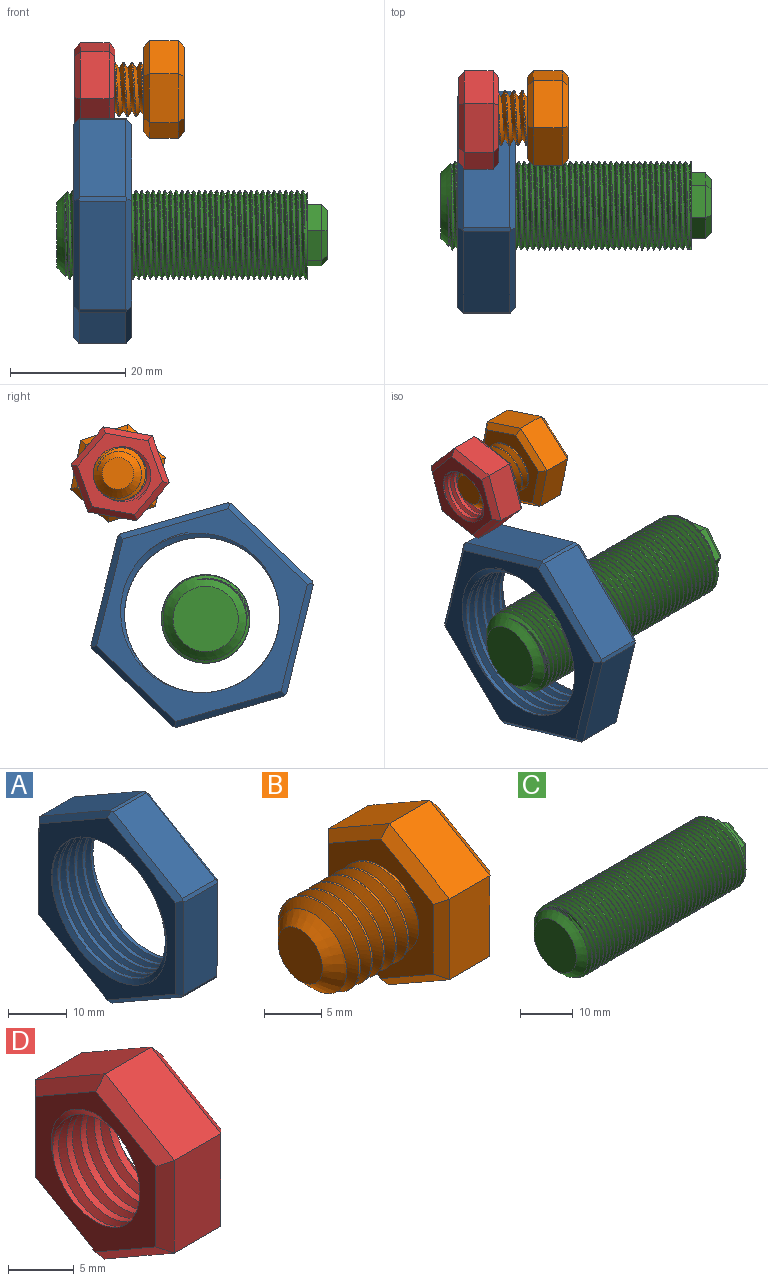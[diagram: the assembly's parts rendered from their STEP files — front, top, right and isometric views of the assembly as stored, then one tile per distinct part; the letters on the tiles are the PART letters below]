
ASSEMBLY  parts=4 mates=2
PART A: 29 faces, bbox 12.4x35.7x40.7 mm
  f0: plane 16.79x9.65mm, normal (0,0.5,0.87), area 154.9mm2, adj f10,f17,f23,f24
  f1: plane 16.75x9.71mm, normal (0,-0.5,0.87), area 154.9mm2, adj f11,f15,f23,f26
  f2: plane 19.36x8mm, normal (0,-1,0), area 154.9mm2, adj f9,f13,f26,f28
  f3: plane 16.79x9.65mm, normal (0,-0.5,-0.87), area 154.9mm2, adj f7,f12,f27,f28
  f4: plane 16.75x9.71mm, normal (0,0.5,-0.87), area 154.9mm2, adj f6,f14,f25,f27
  f5: plane 19.36x8mm, normal (0,1,0), area 154.9mm2, adj f8,f16,f24,f25
  f6: plane 17.31x10.51mm, normal (-0.71,0.35,-0.61), area 27.7mm2, adj f4,f7,f8,f19,f25,f27
  f7: plane 17.34x10.45mm, normal (-0.71,-0.35,-0.61), area 27.7mm2, adj f3,f6,f9,f19,f27,f28
  f8: plane 20x1.04mm, normal (-0.71,0.71,0), area 27.7mm2, adj f5,f6,f10,f19,f24,f25
  f9: plane 20x1.04mm, normal (-0.71,-0.71,0), area 27.7mm2, adj f2,f7,f11,f19,f26,f28
  f10: plane 17.34x10.45mm, normal (-0.71,0.35,0.61), area 27.7mm2, adj f0,f8,f11,f19,f23,f24
  f11: plane 17.31x10.51mm, normal (-0.71,-0.35,0.61), area 27.7mm2, adj f1,f9,f10,f19,f23,f26
  f12: plane 17.34x10.45mm, normal (0.71,-0.35,-0.61), area 27.7mm2, adj f3,f13,f14,f20,f27,f28
  f13: plane 20x1.04mm, normal (0.71,-0.71,0), area 27.7mm2, adj f2,f12,f15,f20,f26,f28
  f14: plane 17.31x10.51mm, normal (0.71,0.35,-0.61), area 27.7mm2, adj f4,f12,f16,f20,f25,f27
  f15: plane 17.31x10.51mm, normal (0.71,-0.35,0.61), area 27.7mm2, adj f1,f13,f17,f20,f23,f26
  f16: plane 20x1.04mm, normal (0.71,0.71,0), area 27.7mm2, adj f5,f14,f17,f20,f24,f25
  f17: plane 17.34x10.45mm, normal (0.71,0.35,0.61), area 27.7mm2, adj f0,f15,f16,f20,f23,f24
  f18: cylinder r=13.48mm len=26.96mm, axis (1,0,0), area 298mm2, adj f19,f20,f21,f22
  f19: plane 38.82x33.75mm, normal (-1,0,0), area 340.7mm2, adj f6,f7,f8,f9,f10,f11,f18,f21
  f20: plane 38.82x33.75mm, normal (1,0,0), area 340.7mm2, adj f12,f13,f14,f15,f16,f17,f18,f21
  f21: bspline ~33.72x29.21mm, area 572.9mm2, adj f18,f19,f20,f22
  f22: bspline ~33.72x29.21mm, area 572.6mm2, adj f18,f19,f20,f21
  f23: cylinder r=20mm len=8.36mm, axis (1,0,0), area 6mm2, adj f0,f1,f10,f11,f15,f17
  f24: cylinder r=20mm len=8.36mm, axis (1,0,0), area 6mm2, adj f0,f5,f8,f10,f16,f17
  f25: cylinder r=20mm len=8.36mm, axis (1,0,0), area 6mm2, adj f4,f5,f6,f8,f14,f16
  f26: cylinder r=20mm len=8.36mm, axis (1,0,0), area 6mm2, adj f1,f2,f9,f11,f13,f15
  f27: cylinder r=20mm len=8.36mm, axis (1,0,0), area 6mm2, adj f3,f4,f6,f7,f12,f14
  f28: cylinder r=20mm len=8.36mm, axis (1,0,0), area 6mm2, adj f2,f3,f7,f9,f12,f13
PART B: 25 faces, bbox 17.8x15.9x18.1 mm
  f0: cylinder r=4.75mm len=9.5mm, axis (1,0,0), area 28.1mm2, adj f1,f2,f4,f12
  f1: bspline ~10.97x9.91mm, area 196.7mm2, adj f0,f2,f4,f12
  f2: bspline ~10.97x10.66mm, area 196.6mm2, adj f0,f1,f4,f12
  f3: plane 5.5x5.5mm, normal (-1,0,0), area 23.8mm2, adj f4
  f4: cone r=4.75mm half-angle=45deg, axis (1,0,0), area 47.4mm2, adj f0,f1,f2,f3
  f5: plane 7.48x5mm, normal (0,-0.5,0.86), area 43.3mm2, adj f6,f10,f18,f22
  f6: plane 8.66x5mm, normal (0,-1,0), area 43.3mm2, adj f5,f7,f16,f20
  f7: plane 7.52x5mm, normal (0,-0.5,-0.87), area 43.3mm2, adj f6,f8,f14,f19
  f8: plane 7.48x5mm, normal (0,0.5,-0.86), area 43.3mm2, adj f7,f9,f13,f21
  f9: plane 8.66x5mm, normal (0,1,0), area 43.3mm2, adj f8,f10,f15,f23
  f10: plane 7.52x5mm, normal (0,0.5,0.87), area 43.3mm2, adj f5,f9,f17,f24
  f11: plane 15.01x13.03mm, normal (1,0,0), area 146.4mm2, adj f13,f14,f15,f16,f17,f18
  f12: plane 15.83x13.85mm, normal (-1,0,0), area 89.2mm2, adj f0,f1,f2,f19,f20,f21,f22,f23
  f13: plane 7.49x4.93mm, normal (0.71,0.36,-0.61), area 11.4mm2, adj f8,f11,f14,f15
  f14: plane 7.52x4.88mm, normal (0.71,-0.35,-0.61), area 11.4mm2, adj f7,f11,f13,f16
  f15: plane 8.66x1.03mm, normal (0.71,0.71,0), area 11.4mm2, adj f9,f11,f13,f17
  f16: plane 8.66x1.03mm, normal (0.71,-0.71,0), area 11.4mm2, adj f6,f11,f14,f18
  f17: plane 7.52x4.88mm, normal (0.71,0.35,0.61), area 11.4mm2, adj f10,f11,f15,f18
  f18: plane 7.49x4.93mm, normal (0.71,-0.36,0.61), area 11.4mm2, adj f5,f11,f16,f17
  f19: plane 7.52x4.88mm, normal (-0.71,-0.35,-0.61), area 11.4mm2, adj f7,f12,f20,f21
  f20: plane 8.66x1.03mm, normal (-0.71,-0.71,0), area 11.4mm2, adj f6,f12,f19,f22
  f21: plane 7.49x4.93mm, normal (-0.71,0.36,-0.61), area 11.4mm2, adj f8,f12,f19,f23
  f22: plane 7.49x4.93mm, normal (-0.71,-0.36,0.61), area 11.4mm2, adj f5,f12,f20,f24
  f23: plane 8.66x1.03mm, normal (-0.71,0.71,0), area 11.4mm2, adj f9,f12,f21,f24
  f24: plane 7.52x4.88mm, normal (-0.71,0.35,0.61), area 11.4mm2, adj f10,f12,f22,f23
PART C: 20 faces, bbox 47.6x18.3x16 mm
  f0: cylinder r=7.68mm len=41.5mm, axis (1,0,0), area 609.8mm2, adj f2,f3,f4,f5,f6
  f1: plane 11.36x11.36mm, normal (-1,0,0), area 101.4mm2, adj f3
  f2: plane 15.97x15.66mm, normal (1,0,0), area 90.9mm2, adj f0,f4,f6,f7,f8,f9,f10,f11
  f3: cone r=7.68mm half-angle=45deg, axis (1,0,0), area 96.9mm2, adj f0,f1,f5,f6
  f4: plane 0.76x0.44mm, normal (0,1,0), area 0.2mm2, adj f0,f2,f5
  f5: bspline ~42.77x17.74mm, area 1672.1mm2, adj f0,f3,f4,f6
  f6: bspline ~42.77x17.74mm, area 1681.9mm2, adj f0,f2,f3,f5
  f7: plane 5.02x2.85mm, normal (0,0.49,0.87), area 14.4mm2, adj f2,f8,f12,f18
  f8: plane 4.98x2.92mm, normal (0,-0.51,0.86), area 14.4mm2, adj f2,f7,f9,f19
  f9: plane 5.77x2.5mm, normal (0,-1,-0.01), area 14.4mm2, adj f2,f8,f10,f17
  f10: plane 5.02x2.85mm, normal (0,-0.49,-0.87), area 14.4mm2, adj f2,f9,f11,f15
  f11: plane 4.98x2.92mm, normal (0,0.51,-0.86), area 14.4mm2, adj f2,f10,f12,f14
  f12: plane 5.77x2.5mm, normal (0,1,0.01), area 14.4mm2, adj f2,f7,f11,f16
  f13: plane 9.24x8.03mm, normal (1,0,0), area 55.4mm2, adj f14,f15,f16,f17,f18,f19
  f14: plane 4.99x3.49mm, normal (0.71,0.36,-0.61), area 7.3mm2, adj f11,f13,f15,f16
  f15: plane 5.02x3.44mm, normal (0.71,-0.35,-0.61), area 7.3mm2, adj f10,f13,f14,f17
  f16: plane 5.77x1.04mm, normal (0.71,0.71,0), area 7.3mm2, adj f12,f13,f14,f18
  f17: plane 5.77x1.04mm, normal (0.71,-0.71,0), area 7.3mm2, adj f9,f13,f15,f19
  f18: plane 5.02x3.44mm, normal (0.71,0.35,0.61), area 7.3mm2, adj f7,f13,f16,f19
  f19: plane 4.99x3.49mm, normal (0.71,-0.36,0.61), area 7.3mm2, adj f8,f13,f17,f18
PART D: 23 faces, bbox 9.1x15.4x17.7 mm
  f0: plane 7.51x5mm, normal (0,0.5,0.87), area 43.3mm2, adj f1,f5,f12,f19
  f1: plane 7.49x5mm, normal (0,-0.5,0.86), area 43.3mm2, adj f0,f2,f13,f17
  f2: plane 8.66x5mm, normal (0,-1,0), area 43.3mm2, adj f1,f3,f11,f15
  f3: plane 7.51x5mm, normal (0,-0.5,-0.87), area 43.3mm2, adj f2,f4,f9,f14
  f4: plane 7.49x5mm, normal (0,0.5,-0.86), area 43.3mm2, adj f3,f5,f8,f16
  f5: plane 8.66x5mm, normal (0,1,0), area 43.3mm2, adj f0,f4,f10,f18
  f6: plane 15.37x13.38mm, normal (-1,0,0), area 71.4mm2, adj f8,f9,f10,f11,f12,f13,f20,f21
  f7: plane 15.37x13.38mm, normal (1,0,0), area 71.4mm2, adj f14,f15,f16,f17,f18,f19,f20,f21
  f8: plane 7.49x4.93mm, normal (-0.71,0.36,-0.61), area 11.4mm2, adj f4,f6,f9,f10
  f9: plane 7.51x4.89mm, normal (-0.71,-0.35,-0.61), area 11.4mm2, adj f3,f6,f8,f11
  f10: plane 8.66x1.02mm, normal (-0.71,0.71,0), area 11.4mm2, adj f5,f6,f8,f12
  f11: plane 8.66x1.02mm, normal (-0.71,-0.71,0), area 11.4mm2, adj f2,f6,f9,f13
  f12: plane 7.51x4.89mm, normal (-0.71,0.35,0.61), area 11.4mm2, adj f0,f6,f10,f13
  f13: plane 7.49x4.93mm, normal (-0.71,-0.36,0.61), area 11.4mm2, adj f1,f6,f11,f12
  f14: plane 7.51x4.89mm, normal (0.71,-0.35,-0.61), area 11.4mm2, adj f3,f7,f15,f16
  f15: plane 8.66x1.02mm, normal (0.71,-0.71,0), area 11.4mm2, adj f2,f7,f14,f17
  f16: plane 7.49x4.93mm, normal (0.71,0.36,-0.61), area 11.4mm2, adj f4,f7,f14,f18
  f17: plane 7.49x4.93mm, normal (0.71,-0.36,0.61), area 11.4mm2, adj f1,f7,f15,f19
  f18: plane 8.66x1.02mm, normal (0.71,0.71,0), area 11.4mm2, adj f5,f7,f16,f19
  f19: plane 7.51x4.89mm, normal (0.71,0.35,0.61), area 11.4mm2, adj f0,f7,f17,f18
  f20: cylinder r=4.66mm len=9.32mm, axis (1,0,0), area 85.4mm2, adj f6,f7,f21,f22
  f21: bspline ~12.5x10.82mm, area 128.5mm2, adj f6,f7,f20,f22
  f22: bspline ~12.5x10.82mm, area 128.4mm2, adj f6,f7,f20,f21
PLACE A rot(axis=(0,0.6,-0.8),180deg) t=(-55.27,-6.86,23.48)mm fixed
PLACE B rot(axis=(1,0,0),71.4deg) t=(-39.66,7.73,48.08)mm
PLACE C rot(axis=(1,0,0),81.1deg) t=(-14.77,-7.48,22.82)mm
PLACE D rot(axis=(1,0,0),100.2deg) t=(-48.16,7.38,48.02)mm fixed
MATE cylindrical C.f0 <-> A.f19  axis (-1,0,0) through (-58.27,-7.48,22.82)mm
MATE cylindrical B.f0 <-> D.f6  axis (-1,0,0) through (-53.16,7.73,48.08)mm
